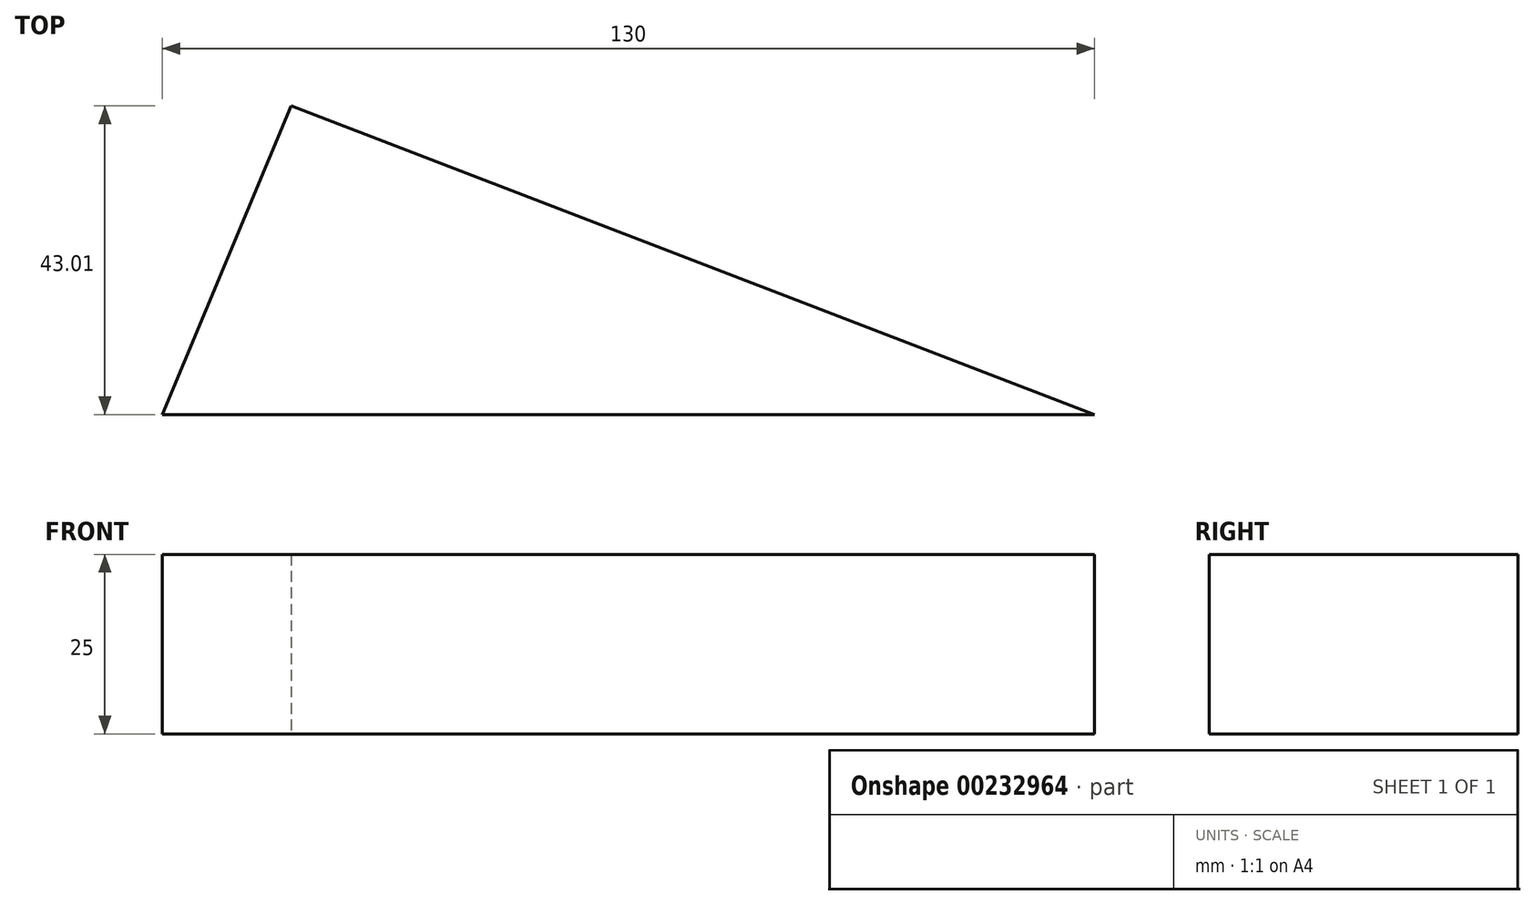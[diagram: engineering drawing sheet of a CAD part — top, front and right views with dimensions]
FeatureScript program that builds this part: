
annotation { "Feature Type Name" : "Feature", "Feature Type Description" : "" }
export const myFeature = defineFeature(function(context is Context, id is Id, definition is map)
    precondition{}
    {
        {
            var Q0;
            Q0=qCreatedBy(makeId("Top.planeOp"),FACE);
            var sketch = newSketch(context, id + "F0", { "sketchPlane" : qUnion([Q0])});
            skLineSegment(sketch, "E0", {"start": v(-108.86, -76.6) * mm, "end": v(21.14, -76.6) * mm});
            skLineSegment(sketch, "E1", {"start": v(-108.86, -76.6) * mm, "end": v(-90.89, -33.6) * mm});
            skLineSegment(sketch, "E2", {"start": v(-90.89, -33.6) * mm, "end": v(21.14, -76.6) * mm});
            skSolve(sketch);
        }
        {
            var Q0;
            Q0=makeQuery(id+"F0.imprint","IMPRINT",FACE,{"disambiguationData":[TD([[makeQuery(id+"F0.imprint","IMPRINT",EDGE,{"derivedFrom":sQuery(id+"F0.wireOp",EDGE,"E0")}),1.0]])]});
            extrude(context, id + "F1", {"entities" : qUnion([Q0]), "depth" : 25 * mm});
        }
    });
